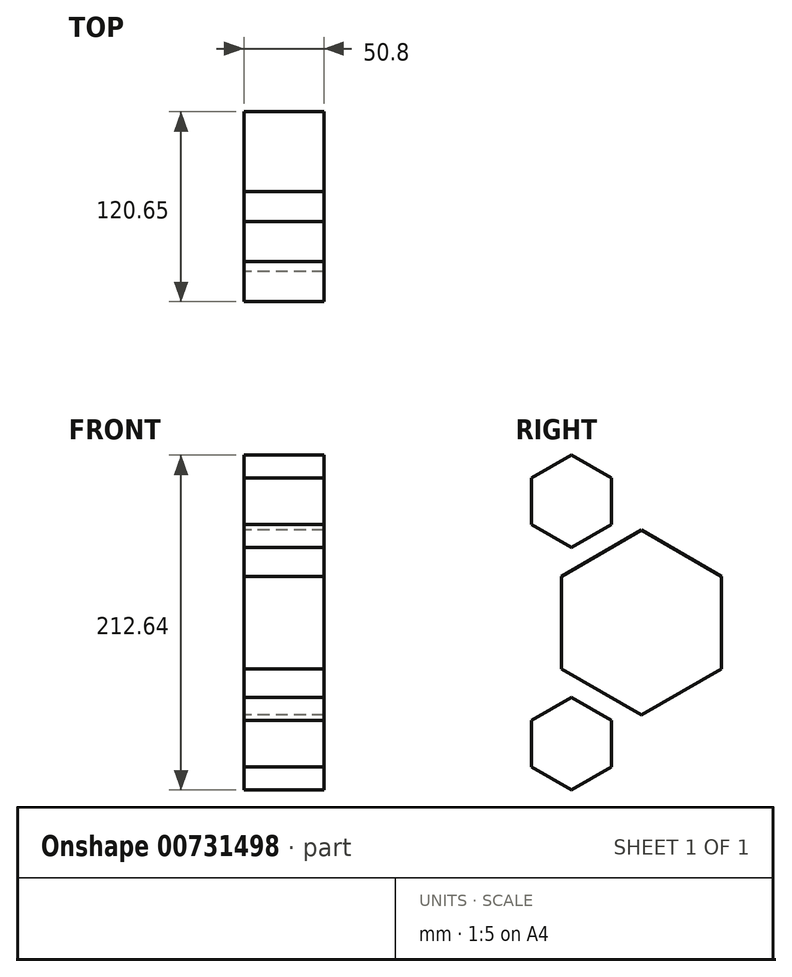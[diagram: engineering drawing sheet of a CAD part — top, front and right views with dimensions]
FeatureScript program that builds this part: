
annotation { "Feature Type Name" : "Feature", "Feature Type Description" : "" }
export const myFeature = defineFeature(function(context is Context, id is Id, definition is map)
    precondition{}
    {
        {
            var Q0;
            Q0=qCreatedBy(makeId("Right.planeOp"),FACE);
            var sketch = newSketch(context, id + "F0", { "sketchPlane" : qUnion([Q0])});
            skCircle(sketch, "E0.cCircle", {"center": v(0, 0) * mm, "radius": 50.8 * mm, "construction": true});
            skLineSegment(sketch, "E0.0", {"start": v(0, 58.66) * mm, "end": v(50.8, 29.33) * mm});
            skLineSegment(sketch, "E0.1", {"start": v(50.8, 29.33) * mm, "end": v(50.8, -29.33) * mm});
            skLineSegment(sketch, "E0.2", {"start": v(50.8, -29.33) * mm, "end": v(0, -58.66) * mm});
            skLineSegment(sketch, "E0.3", {"start": v(0, -58.66) * mm, "end": v(-50.8, -29.33) * mm});
            skLineSegment(sketch, "E0.4", {"start": v(-50.8, -29.33) * mm, "end": v(-50.8, 29.33) * mm});
            skLineSegment(sketch, "E0.5", {"start": v(-50.8, 29.33) * mm, "end": v(0, 58.66) * mm});
            skPoint(sketch, "E0.0.midPoint", {"position": v(25.4, 44) * mm});
            skCircle(sketch, "E1.cCircle", {"center": v(-44.45, -76.99) * mm, "radius": 25.4 * mm, "construction": true});
            skLineSegment(sketch, "E1.0", {"start": v(-44.45, -47.66) * mm, "end": v(-19.05, -62.32) * mm});
            skLineSegment(sketch, "E1.1", {"start": v(-19.05, -62.32) * mm, "end": v(-19.05, -91.65) * mm});
            skLineSegment(sketch, "E1.2", {"start": v(-19.05, -91.65) * mm, "end": v(-44.45, -106.32) * mm});
            skLineSegment(sketch, "E1.3", {"start": v(-44.45, -106.32) * mm, "end": v(-69.85, -91.65) * mm});
            skLineSegment(sketch, "E1.4", {"start": v(-69.85, -91.65) * mm, "end": v(-69.85, -62.32) * mm});
            skLineSegment(sketch, "E1.5", {"start": v(-69.85, -62.32) * mm, "end": v(-44.45, -47.66) * mm});
            skPoint(sketch, "E1.0.midPoint", {"position": v(-31.75, -55) * mm});
            skCircle(sketch, "E2.cCircle", {"center": v(-44.45, 76.99) * mm, "radius": 25.4 * mm, "construction": true});
            skLineSegment(sketch, "E2.0", {"start": v(-44.45, 106.32) * mm, "end": v(-19.05, 91.65) * mm});
            skLineSegment(sketch, "E2.1", {"start": v(-19.05, 91.65) * mm, "end": v(-19.05, 62.32) * mm});
            skLineSegment(sketch, "E2.2", {"start": v(-19.05, 62.32) * mm, "end": v(-44.45, 47.66) * mm});
            skLineSegment(sketch, "E2.3", {"start": v(-44.45, 47.66) * mm, "end": v(-69.85, 62.32) * mm});
            skLineSegment(sketch, "E2.4", {"start": v(-69.85, 62.32) * mm, "end": v(-69.85, 91.65) * mm});
            skLineSegment(sketch, "E2.5", {"start": v(-69.85, 91.65) * mm, "end": v(-44.45, 106.32) * mm});
            skPoint(sketch, "E2.0.midPoint", {"position": v(-31.75, 98.99) * mm});
            skLineSegment(sketch, "E3", {"start": v(-44.45, -76.99) * mm, "end": v(-44.45, 76.99) * mm, "construction": true});
            skLineSegment(sketch, "E4", {"start": v(-44.45, -76.99) * mm, "end": v(0, 0) * mm, "construction": true});
            skLineSegment(sketch, "E5", {"start": v(-44.45, 76.99) * mm, "end": v(0, 0) * mm, "construction": true});
            skLineSegment(sketch, "E6", {"start": v(77.92, 0) * mm, "end": v(-122.45, 0) * mm, "construction": true});
            skPoint(sketch, "E7", {"position": v(50.8, 0) * mm});
            skLineSegment(sketch, "E8", {"start": v(0, 0) * mm, "end": v(-25.4, -44) * mm, "construction": true});
            skSolve(sketch);
        }
        {
            var Q0;
            Q0 = qSketchRegion(id + "F0", true);
            extrude(context, id + "F1", {"entities" : qUnion([Q0]), "depth" : 50.8 * mm, "offsetDistance" : 25.4 * mm});
        }
        {
            var Q0;
            Q0=qCreatedBy(makeId("Top.planeOp"),FACE);
            var sketch = newSketch(context, id + "F2", { "sketchPlane" : qUnion([Q0])});
            skLineSegment(sketch, "E9", {"start": v(80.13, 0) * mm, "end": v(21.47, 101.6) * mm});
            skLineSegment(sketch, "E10", {"start": v(50.8, 0) * mm, "end": v(50.8, 50.8) * mm});
            skLineSegment(sketch, "E11", {"start": v(50.8, 0) * mm, "end": v(80.13, 0) * mm});
            skSolve(sketch);
        }
    });
